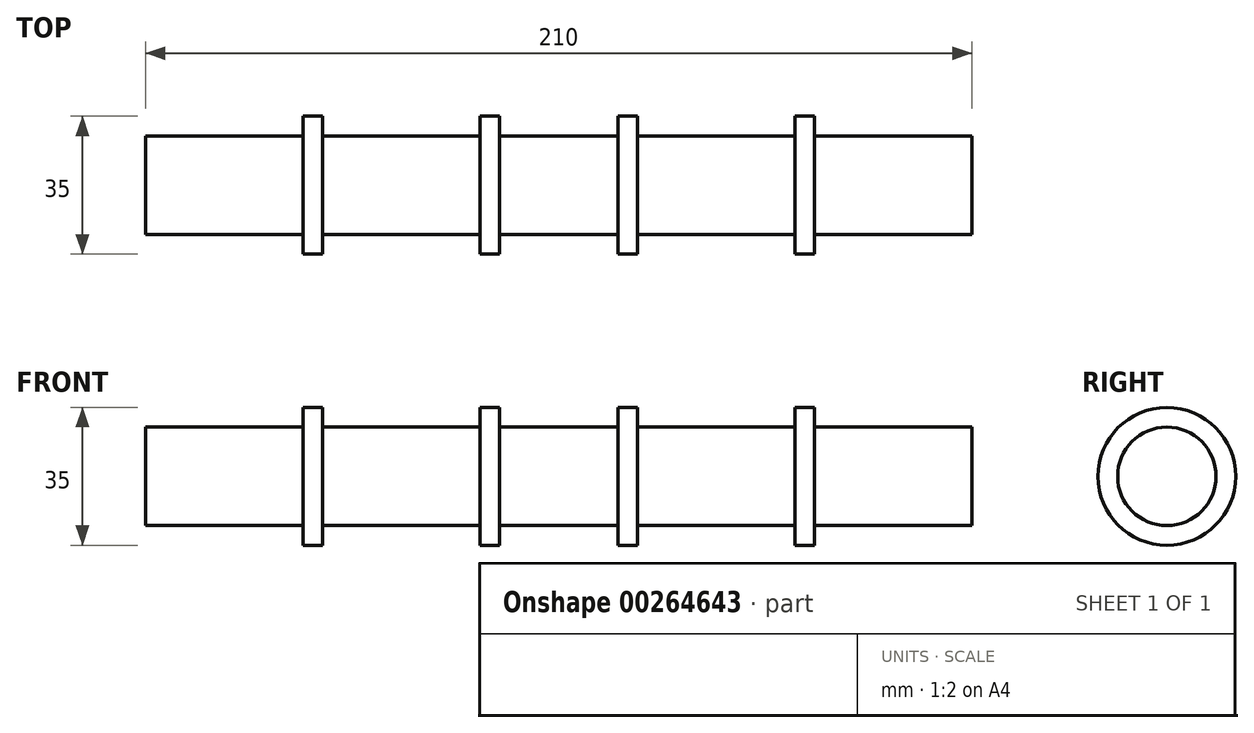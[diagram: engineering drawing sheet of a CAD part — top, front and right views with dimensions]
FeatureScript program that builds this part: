
annotation { "Feature Type Name" : "Feature", "Feature Type Description" : "" }
export const myFeature = defineFeature(function(context is Context, id is Id, definition is map)
    precondition{}
    {
        {
            var Q0;
            Q0=qCreatedBy(makeId("Front.planeOp"),FACE);
            var sketch = newSketch(context, id + "F0", { "sketchPlane" : qUnion([Q0])});
            skLineSegment(sketch, "E0", {"start": v(0, 0) * mm, "end": v(-105, 0) * mm});
            skLineSegment(sketch, "E1", {"start": v(-105, 0) * mm, "end": v(-105, -12.5) * mm});
            skLineSegment(sketch, "E2", {"start": v(-105, -12.5) * mm, "end": v(-65, -12.5) * mm});
            skLineSegment(sketch, "E3", {"start": v(-65, -12.5) * mm, "end": v(-65, -17.5) * mm});
            skLineSegment(sketch, "E4", {"start": v(-65, -17.5) * mm, "end": v(-60, -17.5) * mm});
            skLineSegment(sketch, "E5", {"start": v(-60, -17.5) * mm, "end": v(-60, -12.5) * mm});
            skLineSegment(sketch, "E6", {"start": v(-60, -12.5) * mm, "end": v(-20, -12.5) * mm});
            skLineSegment(sketch, "E7", {"start": v(-20, -12.5) * mm, "end": v(-20, -17.5) * mm});
            skLineSegment(sketch, "E8", {"start": v(-20, -17.5) * mm, "end": v(-15, -17.5) * mm});
            skLineSegment(sketch, "E9", {"start": v(-15, -17.5) * mm, "end": v(-15, -12.5) * mm});
            skLineSegment(sketch, "E10", {"start": v(-15, -12.5) * mm, "end": v(15, -12.5) * mm});
            skLineSegment(sketch, "E11", {"start": v(15, -12.5) * mm, "end": v(15, -17.5) * mm});
            skLineSegment(sketch, "E12", {"start": v(15, -17.5) * mm, "end": v(20, -17.5) * mm});
            skLineSegment(sketch, "E13", {"start": v(20, -17.5) * mm, "end": v(20, -12.5) * mm});
            skLineSegment(sketch, "E14", {"start": v(20, -12.5) * mm, "end": v(60, -12.5) * mm});
            skLineSegment(sketch, "E15", {"start": v(60, -12.5) * mm, "end": v(60, -17.5) * mm});
            skLineSegment(sketch, "E16", {"start": v(60, -17.5) * mm, "end": v(65, -17.5) * mm});
            skLineSegment(sketch, "E17", {"start": v(65, -17.5) * mm, "end": v(65, -12.5) * mm});
            skLineSegment(sketch, "E18", {"start": v(65, -12.5) * mm, "end": v(105, -12.5) * mm});
            skLineSegment(sketch, "E19", {"start": v(105, -12.5) * mm, "end": v(105, 0) * mm});
            skLineSegment(sketch, "E20", {"start": v(105, 0) * mm, "end": v(0, 0) * mm});
            skLineSegment(sketch, "E21", {"start": v(-40, -12.5) * mm, "end": v(-40, -44.07) * mm, "construction": true});
            skLineSegment(sketch, "E22", {"start": v(40, -12.5) * mm, "end": v(40, -44.07) * mm, "construction": true});
            skLineSegment(sketch, "E23", {"start": v(40, -44.07) * mm, "end": v(-40, -44.07) * mm, "construction": true});
            skSolve(sketch);
        }
        {
            var Q0;
            Q0=makeQuery(id+"F0.imprint","IMPRINT",FACE,{"disambiguationData":[TD([[makeQuery(id+"F0.imprint","IMPRINT",EDGE,{"derivedFrom":sQuery(id+"F0.wireOp",EDGE,"E0")}),1.0]])]});
            var Q1;
            Q1=sQuery(id+"F0.wireOp",EDGE,"E0");
            revolve(context, id + "F1", {"entities" : qUnion([Q0]), "axis" : qUnion([Q1]), "revolveType" : RevolveType.FULL});
        }
    });
